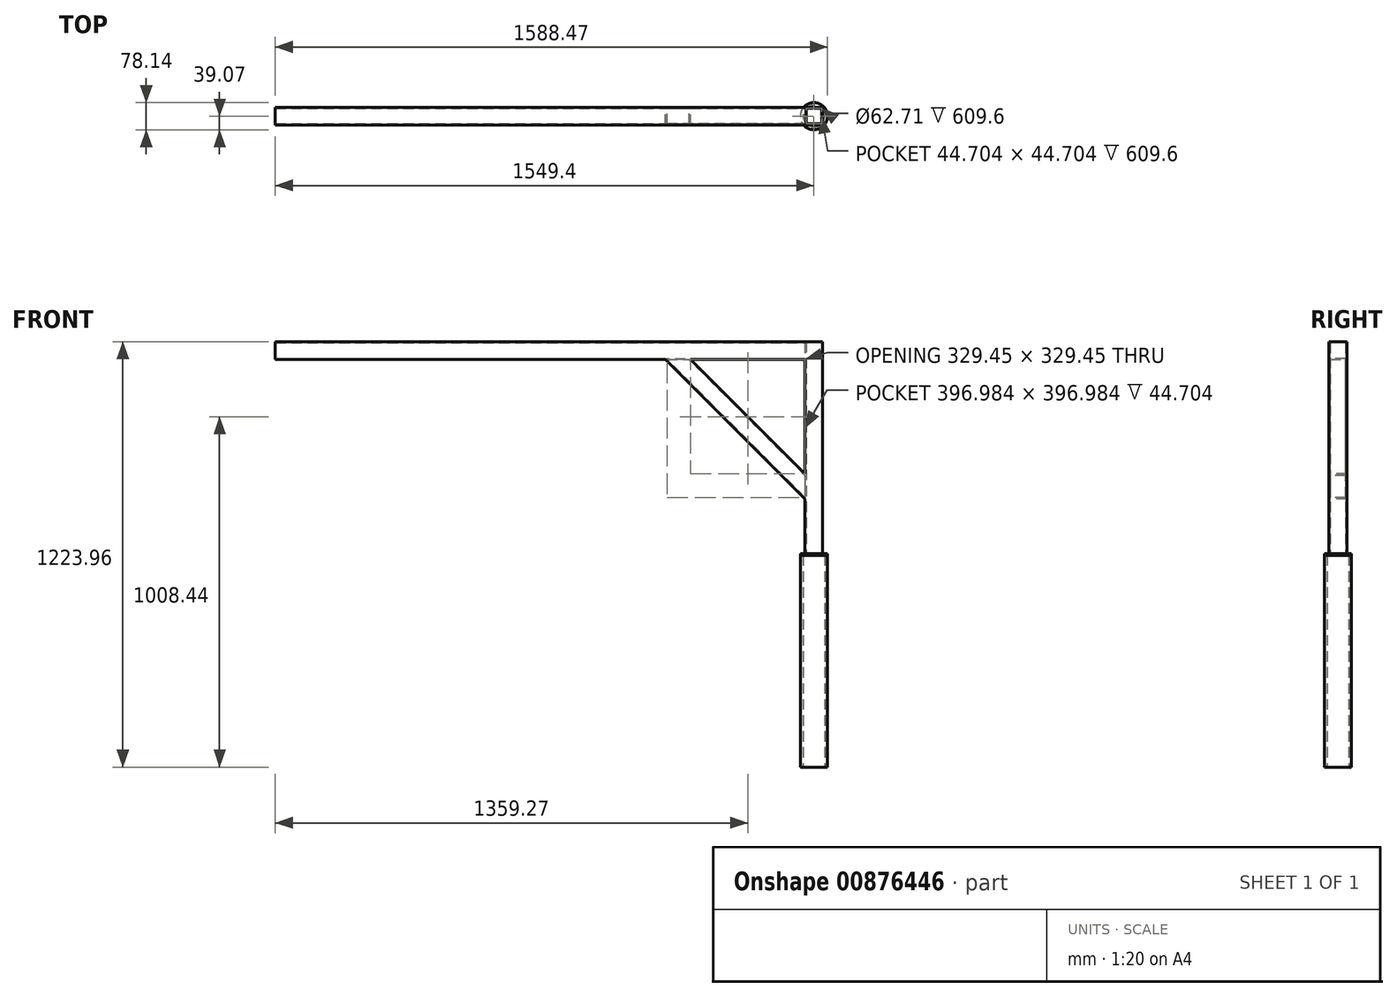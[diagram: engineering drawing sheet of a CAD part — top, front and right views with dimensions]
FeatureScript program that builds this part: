
annotation { "Feature Type Name" : "Feature", "Feature Type Description" : "" }
export const myFeature = defineFeature(function(context is Context, id is Id, definition is map)
    precondition{}
    {
        {
            var Q0;
            Q0=qCreatedBy(makeId("Top.planeOp"),FACE);
            var sketch = newSketch(context, id + "F0", { "sketchPlane" : qUnion([Q0])});
            skCircle(sketch, "E0", {"center": v(0, 0) * mm, "radius": 38.92 * mm});
            skCircle(sketch, "E1", {"center": v(0, 0) * mm, "radius": 31.36 * mm});
            skSolve(sketch);
        }
        {
            var Q0;
            Q0=makeQuery(id+"F0.imprint","IMPRINT",FACE,{"disambiguationData":[TD([[makeQuery(id+"F0.imprint","IMPRINT",EDGE,{"derivedFrom":sQuery(id+"F0.wireOp",EDGE,"E0")}),1.0]])]});
            extrude(context, id + "F1", {"entities" : qUnion([Q0]), "depth" : 609.6 * mm, "offsetDistance" : 25.4 * mm});
        }
        {
            var Q0;
            Q0=makeQuery(id+"F1.opExtrude","CAP_FACE",FACE,{"disambiguationData":[OSD([sQuery(id+"F0.wireOp",EDGE,"E0"),sQuery(id+"F0.wireOp",EDGE,"E1")])],"isStart":false});
            var sketch = newSketch(context, id + "F2", { "sketchPlane" : qUnion([Q0])});
            skCircle(sketch, "E2", {"center": v(0, 0) * mm, "radius": 39.07 * mm});
            skSolve(sketch);
        }
        {
            var Q0;
            Q0 = qSketchRegion(id + "F2", true);
            extrude(context, id + "F3", {"entities" : qUnion([Q0]), "operationType" : NewBodyOperationType.ADD, "depth" : 4.76 * mm, "offsetDistance" : 25.4 * mm});
        }
        {
            var Q0;
            Q0=makeQuery(id+"F3.opExtrude","CAP_FACE",FACE,{"disambiguationData":[OSD([sQuery(id+"F2.wireOp",EDGE,"E2")])],"isStart":false});
            var sketch = newSketch(context, id + "F4", { "sketchPlane" : qUnion([Q0])});
            skLineSegment(sketch, "E3.bottom", {"start": v(-25.4, 25.4) * mm, "end": v(25.4, 25.4) * mm});
            skLineSegment(sketch, "E3.top", {"start": v(-25.4, -25.4) * mm, "end": v(25.4, -25.4) * mm});
            skLineSegment(sketch, "E3.left", {"start": v(-25.4, 25.4) * mm, "end": v(-25.4, -25.4) * mm});
            skLineSegment(sketch, "E3.right", {"start": v(25.4, 25.4) * mm, "end": v(25.4, -25.4) * mm});
            skLineSegment(sketch, "E4", {"start": v(-25.4, 25.4) * mm, "end": v(25.4, -25.4) * mm, "construction": true});
            skLineSegment(sketch, "E5", {"start": v(25.4, 25.4) * mm, "end": v(-25.4, -25.4) * mm, "construction": true});
            skPoint(sketch, "E6", {"position": v(0, 0) * mm});
            skLineSegment(sketch, "E7.bottom", {"start": v(-22.35, 22.35) * mm, "end": v(22.35, 22.35) * mm});
            skLineSegment(sketch, "E7.top", {"start": v(-22.35, -22.35) * mm, "end": v(22.35, -22.35) * mm});
            skLineSegment(sketch, "E7.left", {"start": v(-22.35, 22.35) * mm, "end": v(-22.35, -22.35) * mm});
            skLineSegment(sketch, "E7.right", {"start": v(22.35, 22.35) * mm, "end": v(22.35, -22.35) * mm});
            skLineSegment(sketch, "E8", {"start": v(-22.35, 22.35) * mm, "end": v(22.35, -22.35) * mm, "construction": true});
            skLineSegment(sketch, "E9", {"start": v(-22.35, -22.35) * mm, "end": v(22.35, 22.35) * mm, "construction": true});
            skSolve(sketch);
        }
        {
            var Q0;
            Q0 = qSketchRegion(id + "F4", true);
            extrude(context, id + "F5", {"entities" : qUnion([Q0]), "operationType" : NewBodyOperationType.ADD, "depth" : 609.6 * mm, "offsetDistance" : 25.4 * mm});
        }
        {
            var Q0;
            Q0=makeQuery(id+"F5.opExtrude","SWEPT_FACE",FACE,{"disambiguationData":[OSD([sQuery(id+"F4.wireOp",EDGE,"E3.left")])]});
            var sketch = newSketch(context, id + "F6", { "sketchPlane" : qUnion([Q0])});
            skLineSegment(sketch, "E10.bottom", {"start": v(-25.4, 1223.96) * mm, "end": v(25.4, 1223.96) * mm});
            skLineSegment(sketch, "E10.top", {"start": v(-25.4, 1173.16) * mm, "end": v(25.4, 1173.16) * mm});
            skLineSegment(sketch, "E10.left", {"start": v(-25.4, 1223.96) * mm, "end": v(-25.4, 1173.16) * mm});
            skLineSegment(sketch, "E10.right", {"start": v(25.4, 1223.96) * mm, "end": v(25.4, 1173.16) * mm});
            skLineSegment(sketch, "E11", {"start": v(-25.4, 1223.96) * mm, "end": v(25.4, 1173.16) * mm, "construction": true});
            skPoint(sketch, "E12", {"position": v(0, 1198.56) * mm});
            skLineSegment(sketch, "E13", {"start": v(-25.4, 1173.16) * mm, "end": v(25.4, 1223.96) * mm, "construction": true});
            skLineSegment(sketch, "E14.bottom", {"start": v(-22.35, 1220.91) * mm, "end": v(22.35, 1220.91) * mm});
            skLineSegment(sketch, "E14.top", {"start": v(-22.35, 1176.21) * mm, "end": v(22.35, 1176.21) * mm});
            skLineSegment(sketch, "E14.left", {"start": v(-22.35, 1220.91) * mm, "end": v(-22.35, 1176.21) * mm});
            skLineSegment(sketch, "E14.right", {"start": v(22.35, 1220.91) * mm, "end": v(22.35, 1176.21) * mm});
            skLineSegment(sketch, "E15", {"start": v(-22.35, 1220.91) * mm, "end": v(22.35, 1176.21) * mm, "construction": true});
            skLineSegment(sketch, "E16", {"start": v(22.35, 1220.91) * mm, "end": v(-22.35, 1176.21) * mm, "construction": true});
            skSolve(sketch);
        }
        {
            var Q0;
            Q0 = qSketchRegion(id + "F6", true);
            extrude(context, id + "F7", {"entities" : qUnion([Q0]), "operationType" : NewBodyOperationType.ADD, "depth" : 1524 * mm, "offsetDistance" : 25.4 * mm});
        }
        {
            var Q0;
            Q0=makeQuery(id+"F7.opExtrude","CAP_EDGE",EDGE,{"disambiguationData":[OSD([sQuery(id+"F6.wireOp",EDGE,"E10.top")])],"isStart":true});
            var Q1;
            Q1=makeQuery(id+"F7.boolean.opBoolean","SPLIT",FACE,{"disambiguationData":[TD([makeQuery(id+"F3.opExtrude","CAP_FACE",FACE,{"disambiguationData":[OSD([sQuery(id+"F2.wireOp",EDGE,"E2")])],"isStart":false})])],"derivedFrom":makeQuery(id+"F5.opExtrude","SWEPT_FACE",FACE,{"disambiguationData":[OSD([sQuery(id+"F4.wireOp",EDGE,"E3.left")])]})});
            cPlane(context, id + "F8", {"entities" : qUnion([Q0, Q1]), "cplaneType" : CPlaneType.LINE_ANGLE, "offset" : 25.4 * mm, "angle" : 45 * degree, "oppositeDirection" : true, "width" : 152.4 * mm, "height" : 152.4 * mm});
        }
        {
            var Q0;
            Q0=qCreatedBy(id+"F8.planeOp",FACE);
            var sketch = newSketch(context, id + "F9", { "sketchPlane" : qUnion([Q0])});
            skLineSegment(sketch, "E17.0", {"start": v(25.4, -230.12) * mm, "end": v(25.4, 883.43) * mm, "construction": true});
            skLineSegment(sketch, "E17.1", {"start": v(-25.4, -230.12) * mm, "end": v(-25.4, 883.43) * mm, "construction": true});
            skLineSegment(sketch, "E18.bottom", {"start": v(25.4, 578.63) * mm, "end": v(-25.4, 578.63) * mm});
            skLineSegment(sketch, "E18.top", {"start": v(25.4, 527.83) * mm, "end": v(-25.4, 527.83) * mm});
            skLineSegment(sketch, "E18.left", {"start": v(25.4, 578.63) * mm, "end": v(25.4, 527.83) * mm});
            skLineSegment(sketch, "E18.right", {"start": v(-25.4, 578.63) * mm, "end": v(-25.4, 527.83) * mm});
            skLineSegment(sketch, "E19", {"start": v(25.4, 578.63) * mm, "end": v(-25.4, 527.83) * mm, "construction": true});
            skLineSegment(sketch, "E20", {"start": v(-25.4, 578.63) * mm, "end": v(25.4, 527.83) * mm, "construction": true});
            skPoint(sketch, "E21", {"position": v(0, 553.23) * mm});
            skLineSegment(sketch, "E22.bottom", {"start": v(22.35, 575.58) * mm, "end": v(-22.35, 575.58) * mm});
            skLineSegment(sketch, "E22.top", {"start": v(22.35, 530.88) * mm, "end": v(-22.35, 530.88) * mm});
            skLineSegment(sketch, "E22.left", {"start": v(22.35, 575.58) * mm, "end": v(22.35, 530.88) * mm});
            skLineSegment(sketch, "E22.right", {"start": v(-22.35, 575.58) * mm, "end": v(-22.35, 530.88) * mm});
            skLineSegment(sketch, "E23", {"start": v(22.35, 575.58) * mm, "end": v(-22.35, 530.88) * mm, "construction": true});
            skLineSegment(sketch, "E24", {"start": v(-22.35, 575.58) * mm, "end": v(22.35, 530.88) * mm, "construction": true});
            skSolve(sketch);
        }
        {
            var Q0;
            Q0 = qSketchRegion(id + "F9", true);
            var Q1;
            Q1=makeQuery(id+"F7.boolean.opBoolean","SPLIT",FACE,{"disambiguationData":[TD([makeQuery(id+"F3.opExtrude","CAP_FACE",FACE,{"disambiguationData":[OSD([sQuery(id+"F2.wireOp",EDGE,"E2")])],"isStart":false})])],"derivedFrom":makeQuery(id+"F5.opExtrude","SWEPT_FACE",FACE,{"disambiguationData":[OSD([sQuery(id+"F4.wireOp",EDGE,"E3.left")])]})});
            var Q2;
            Q2=makeQuery(id+"F7.opExtrude","SWEPT_FACE",FACE,{"disambiguationData":[OSD([sQuery(id+"F6.wireOp",EDGE,"E10.top")])]});
            extrude(context, id + "F10", {"entities" : qUnion([Q0]), "operationType" : NewBodyOperationType.ADD, "endBound" : BoundingType.UP_TO_SURFACE, "depth" : 25.4 * mm, "endBoundEntityFace" : qUnion([Q1]), "offsetDistance" : 25.4 * mm, "hasSecondDirection" : true, "secondDirectionBound" : SecondDirectionBoundingType.UP_TO_SURFACE, "secondDirectionOppositeDirection" : true, "secondDirectionDepth" : 25.4 * mm, "secondDirectionBoundEntityFace" : qUnion([Q2])});
        }
    });
